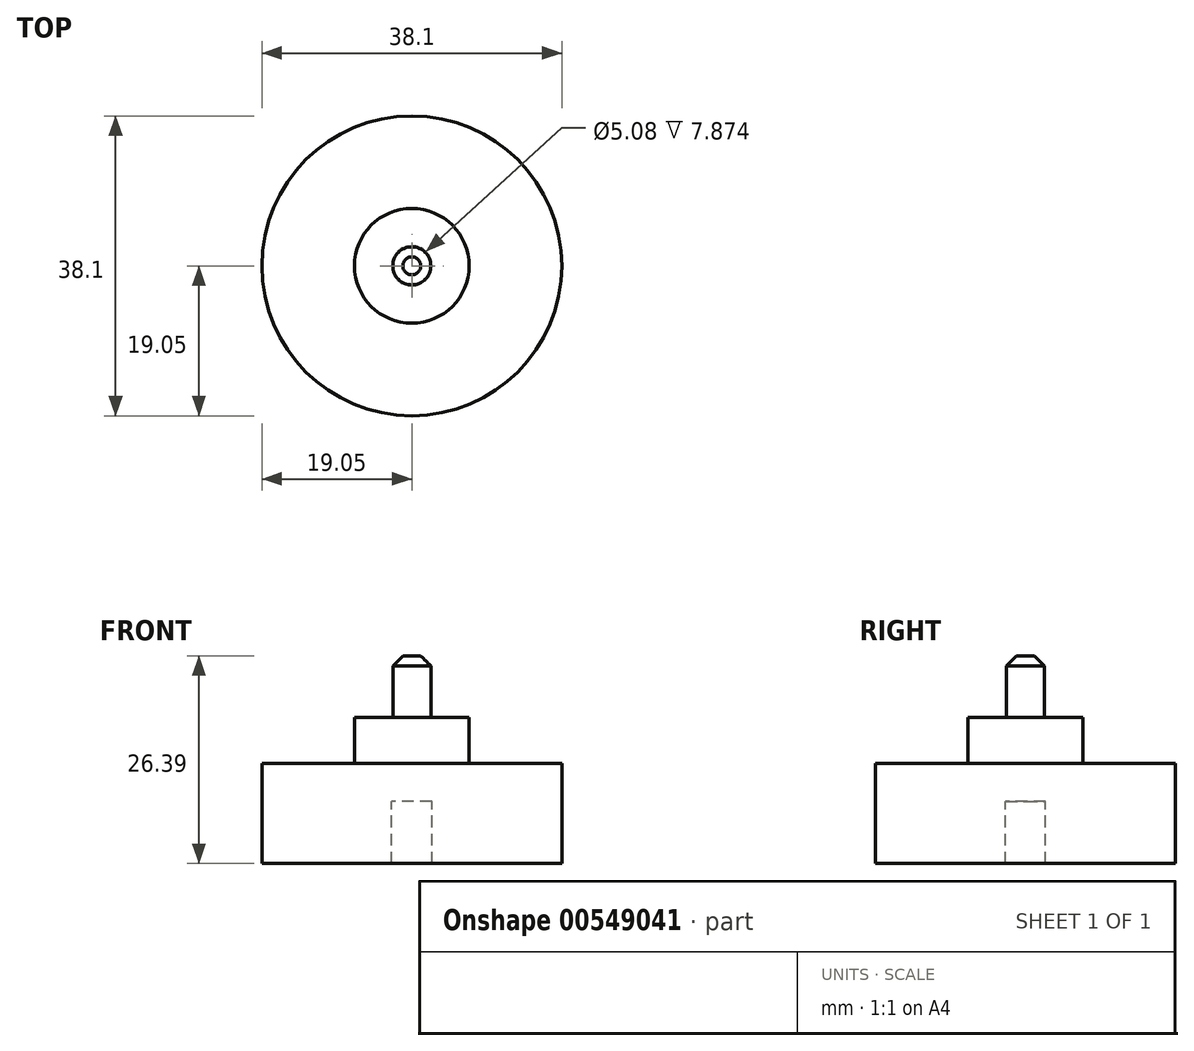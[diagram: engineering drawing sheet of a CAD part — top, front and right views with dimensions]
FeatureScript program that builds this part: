
annotation { "Feature Type Name" : "Feature", "Feature Type Description" : "" }
export const myFeature = defineFeature(function(context is Context, id is Id, definition is map)
    precondition{}
    {
        {
            var Q0;
            Q0=qCreatedBy(makeId("Front.planeOp"),FACE);
            var sketch = newSketch(context, id + "F0", { "sketchPlane" : qUnion([Q0])});
            skLineSegment(sketch, "E0", {"start": v(19.05, 0) * mm, "end": v(19.05, 12.7) * mm});
            skLineSegment(sketch, "E1", {"start": v(19.05, 12.7) * mm, "end": v(7.29, 12.7) * mm});
            skLineSegment(sketch, "E2", {"start": v(2.41, 18.54) * mm, "end": v(7.29, 18.54) * mm});
            skLineSegment(sketch, "E3", {"start": v(7.29, 18.54) * mm, "end": v(7.29, 12.7) * mm});
            skLineSegment(sketch, "E4", {"start": v(2.54, 0) * mm, "end": v(2.54, 7.87) * mm});
            skLineSegment(sketch, "E5", {"start": v(2.54, 7.87) * mm, "end": v(0, 7.87) * mm});
            skLineSegment(sketch, "E6", {"start": v(2.54, 0) * mm, "end": v(19.05, 0) * mm});
            skLineSegment(sketch, "E7", {"start": v(0, 26.4) * mm, "end": v(2.41, 26.4) * mm});
            skLineSegment(sketch, "E8", {"start": v(2.41, 26.4) * mm, "end": v(2.41, 18.54) * mm});
            skPoint(sketch, "E9.start.orphan", {"position": v(0, 18.54) * mm});
            skLineSegment(sketch, "E10", {"start": v(0, 26.4) * mm, "end": v(0, 7.87) * mm});
            skSolve(sketch);
        }
        {
            var Q0;
            Q0 = qSketchRegion(id + "F0", true);
            var Q1;
            Q1=sQuery(id+"F0.wireOp",EDGE,"E10");
            revolve(context, id + "F1", {"entities" : qUnion([Q0]), "axis" : qUnion([Q1]), "revolveType" : RevolveType.FULL});
        }
        {
            var Q0;
            Q0=makeQuery(id+"F1.opRevolve","SWEPT_EDGE",EDGE,{"disambiguationData":[OSD([sQuery(id+"F0.wireOp",EDGE,"E7"),sQuery(id+"F0.wireOp",EDGE,"E8")])]});
            chamfer(context, id + "F2", {"entities" : qUnion([Q0]), "width" : 1.27 * mm, "tangentPropagation" : true});
        }
    });
